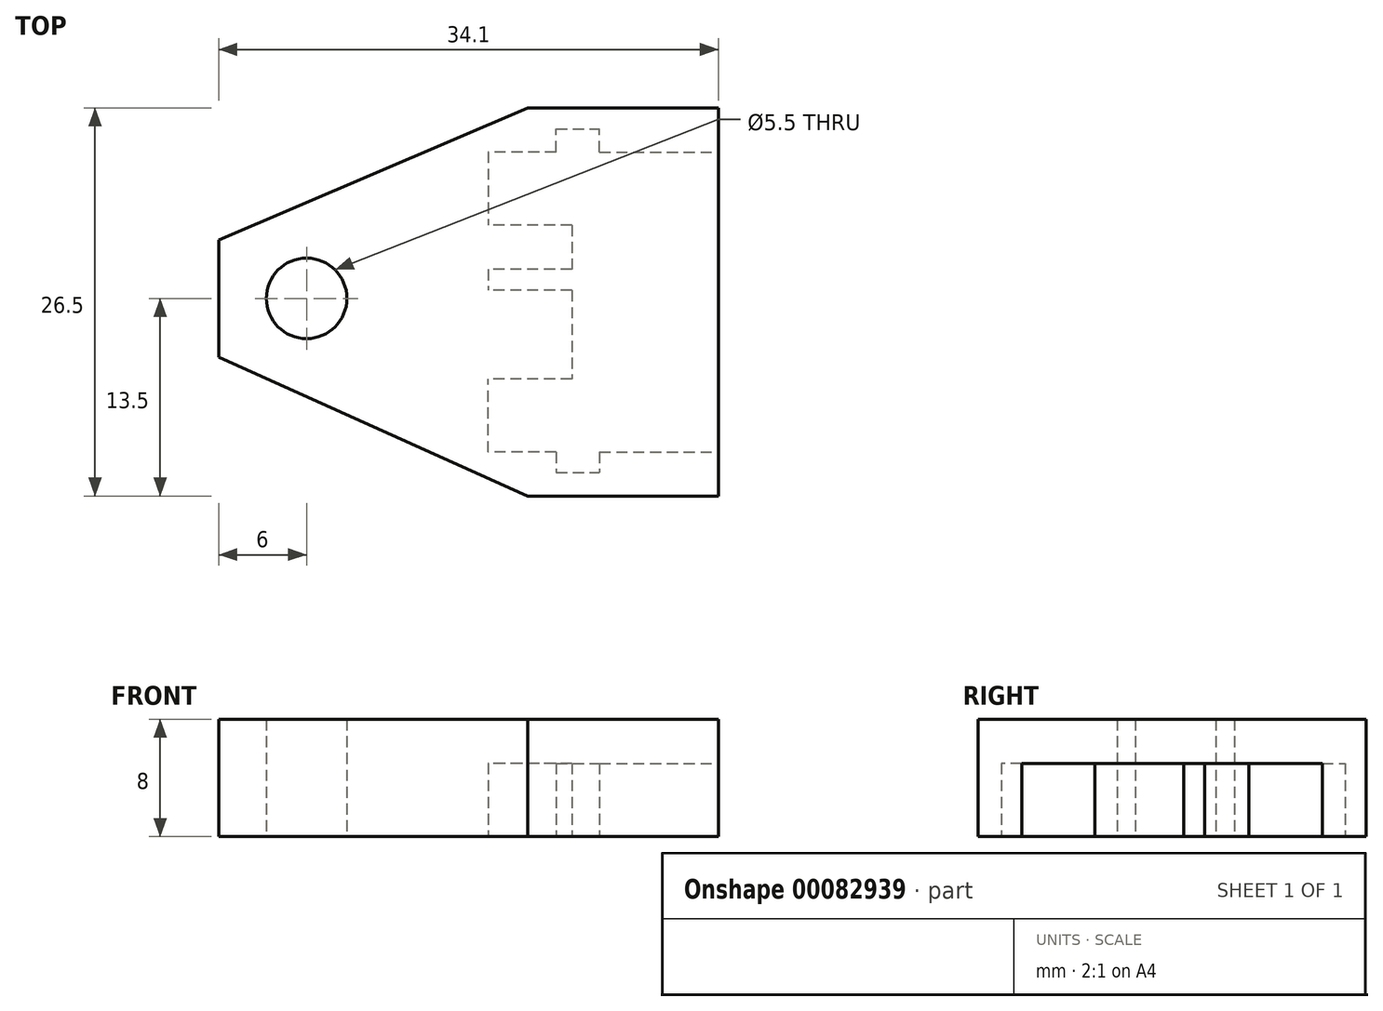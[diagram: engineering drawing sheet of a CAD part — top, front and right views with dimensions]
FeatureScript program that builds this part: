
annotation { "Feature Type Name" : "Feature", "Feature Type Description" : "" }
export const myFeature = defineFeature(function(context is Context, id is Id, definition is map)
    precondition{}
    {
        {
            var Q0;
            Q0=qCreatedBy(makeId("Top.planeOp"),FACE);
            var sketch = newSketch(context, id + "F0", { "sketchPlane" : qUnion([Q0])});
            skCircle(sketch, "E0", {"center": v(0, 0) * mm, "radius": 2.75 * mm});
            skLineSegment(sketch, "E1.bottom", {"start": v(20, 10) * mm, "end": v(28.1, 10) * mm});
            skLineSegment(sketch, "E1.top", {"start": v(20, -10.5) * mm, "end": v(28.1, -10.5) * mm});
            skLineSegment(sketch, "E1.left", {"start": v(18.1, 5) * mm, "end": v(18.1, 1.99) * mm});
            skLineSegment(sketch, "E2", {"start": v(28.1, -13.5) * mm, "end": v(15.1, -13.5) * mm});
            skLineSegment(sketch, "E3", {"start": v(15.1, -13.5) * mm, "end": v(-6, -4) * mm});
            skLineSegment(sketch, "E4", {"start": v(-6, -4) * mm, "end": v(-6, 4) * mm});
            skLineSegment(sketch, "E5", {"start": v(-6, 4) * mm, "end": v(15.1, 13) * mm});
            skLineSegment(sketch, "E6", {"start": v(15.1, 13) * mm, "end": v(28.1, 13) * mm});
            skLineSegment(sketch, "E7", {"start": v(28.1, 13) * mm, "end": v(28.1, 10) * mm});
            skLineSegment(sketch, "E8", {"start": v(28.1, -10.5) * mm, "end": v(28.1, -13.5) * mm});
            skLineSegment(sketch, "E9.bottom", {"start": v(17.03, 10) * mm, "end": v(12.39, 10) * mm});
            skLineSegment(sketch, "E9.top", {"start": v(18.1, 5) * mm, "end": v(12.39, 5) * mm});
            skLineSegment(sketch, "E9.right", {"start": v(12.39, 10) * mm, "end": v(12.39, 5) * mm});
            skLineSegment(sketch, "E10.bottom", {"start": v(17.03, -10.5) * mm, "end": v(12.39, -10.5) * mm});
            skLineSegment(sketch, "E10.top", {"start": v(18.1, -5.5) * mm, "end": v(12.39, -5.5) * mm});
            skLineSegment(sketch, "E10.right", {"start": v(12.39, -10.5) * mm, "end": v(12.39, -5.5) * mm});
            skLineSegment(sketch, "E11.bottom", {"start": v(18.1, 1.99) * mm, "end": v(12.39, 1.99) * mm});
            skLineSegment(sketch, "E11.top", {"start": v(18.1, 0.54) * mm, "end": v(12.39, 0.54) * mm});
            skLineSegment(sketch, "E11.right", {"start": v(12.39, 1.99) * mm, "end": v(12.39, 0.54) * mm});
            skLineSegment(sketch, "E12.trimOffspring", {"start": v(18.1, 0.54) * mm, "end": v(18.1, -5.5) * mm});
            skLineSegment(sketch, "E13.top", {"start": v(17.03, 11.57) * mm, "end": v(20, 11.57) * mm});
            skLineSegment(sketch, "E13.left", {"start": v(17.03, 10) * mm, "end": v(17.03, 11.57) * mm});
            skLineSegment(sketch, "E13.right", {"start": v(20, 10) * mm, "end": v(20, 11.57) * mm});
            skLineSegment(sketch, "E14.top", {"start": v(17.03, -11.9) * mm, "end": v(20, -11.9) * mm});
            skLineSegment(sketch, "E14.left", {"start": v(17.03, -10.5) * mm, "end": v(17.03, -11.9) * mm});
            skLineSegment(sketch, "E14.right", {"start": v(20, -10.5) * mm, "end": v(20, -11.9) * mm});
            skSolve(sketch);
        }
        {
            var Q0;
            Q0 = qSketchRegion(id + "F0", true);
            extrude(context, id + "F1", {"entities" : qUnion([Q0]), "depth" : 5 * mm});
        }
        {
            var Q0;
            Q0=makeQuery(id+"F1.opExtrude","CAP_FACE",FACE,{"disambiguationData":[OSD([sQuery(id+"F0.wireOp",EDGE,"E0"),sQuery(id+"F0.wireOp",EDGE,"E1.bottom"),sQuery(id+"F0.wireOp",EDGE,"E1.top"),sQuery(id+"F0.wireOp",EDGE,"E1.left"),sQuery(id+"F0.wireOp",EDGE,"E2"),sQuery(id+"F0.wireOp",EDGE,"E3"),sQuery(id+"F0.wireOp",EDGE,"E4"),sQuery(id+"F0.wireOp",EDGE,"E5"),sQuery(id+"F0.wireOp",EDGE,"E6"),sQuery(id+"F0.wireOp",EDGE,"E7"),sQuery(id+"F0.wireOp",EDGE,"E8"),sQuery(id+"F0.wireOp",EDGE,"E9.bottom"),sQuery(id+"F0.wireOp",EDGE,"E9.top"),sQuery(id+"F0.wireOp",EDGE,"E9.right"),sQuery(id+"F0.wireOp",EDGE,"E10.bottom"),sQuery(id+"F0.wireOp",EDGE,"E10.top"),sQuery(id+"F0.wireOp",EDGE,"E10.right"),sQuery(id+"F0.wireOp",EDGE,"E11.bottom"),sQuery(id+"F0.wireOp",EDGE,"E11.top"),sQuery(id+"F0.wireOp",EDGE,"E11.right"),sQuery(id+"F0.wireOp",EDGE,"E12.trimOffspring")])],"isStart":false});
            var sketch = newSketch(context, id + "F2", { "sketchPlane" : qUnion([Q0])});
            skLineSegment(sketch, "E15", {"start": v(-6, 4) * mm, "end": v(15.1, 13) * mm});
            skLineSegment(sketch, "E16", {"start": v(15.1, 13) * mm, "end": v(28.1, 13) * mm});
            skLineSegment(sketch, "E17", {"start": v(28.1, 13) * mm, "end": v(28.1, -13.5) * mm});
            skLineSegment(sketch, "E18", {"start": v(28.1, -13.5) * mm, "end": v(15.1, -13.5) * mm});
            skLineSegment(sketch, "E19", {"start": v(15.1, -13.5) * mm, "end": v(-6, -4) * mm});
            skLineSegment(sketch, "E20", {"start": v(-6, -4) * mm, "end": v(-6, 4) * mm});
            skCircle(sketch, "E21", {"center": v(0, 0) * mm, "radius": 2.75 * mm});
            skSolve(sketch);
        }
        {
            var Q0;
            Q0 = qSketchRegion(id + "F2", true);
            extrude(context, id + "F3", {"entities" : qUnion([Q0]), "operationType" : NewBodyOperationType.ADD, "depth" : 3 * mm});
        }
    });
